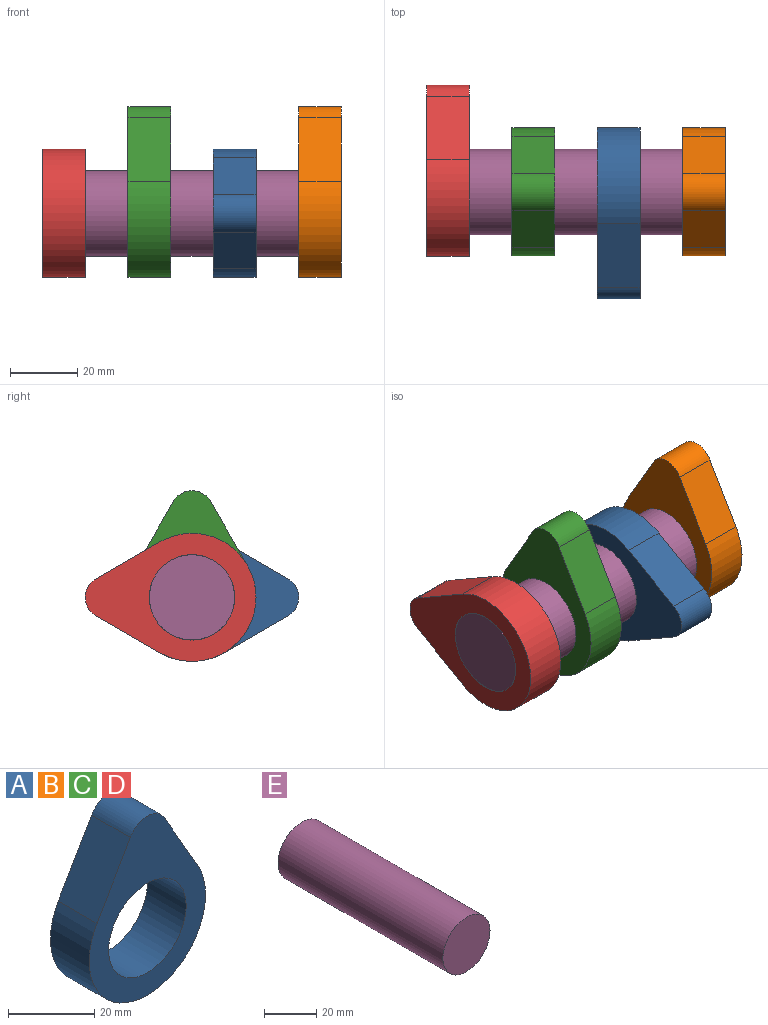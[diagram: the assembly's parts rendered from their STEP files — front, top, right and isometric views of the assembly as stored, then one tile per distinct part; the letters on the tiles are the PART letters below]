
ASSEMBLY  parts=5 mates=4
PART A: 7 faces, bbox 38.1x12.7x50.8 mm
  f0: cylinder r=6.35mm len=12.7mm, axis (0,1,0), area 173.1mm2, adj f1,f4,f5,f6
  f1: plane 18.9x12.7mm, normal (-0.87,0,0.5), area 277.2mm2, adj f0,f2,f5,f6
  f2: cylinder r=19.05mm len=38.1mm, axis (0,1,0), area 1013.5mm2, adj f1,f4,f5,f6
  f3: cylinder r=12.7mm len=25.4mm, axis (0,1,0), area 1013.4mm2, adj f5,f6
  f4: plane 18.9x12.7mm, normal (0.87,0,0.5), area 277.2mm2, adj f0,f2,f5,f6
  f5: plane 50.8x38.1mm, normal (0,-1,0), area 854.3mm2, adj f0,f1,f2,f3,f4
  f6: plane 50.8x38.1mm, normal (0,1,0), area 854.3mm2, adj f0,f1,f2,f3,f4
PART B: same geometry as A
PART C: same geometry as A
PART D: same geometry as A
PART E: 3 faces, bbox 25.4x88.9x25.4 mm
  f0: cylinder r=12.7mm len=88.9mm, axis (0,1,0), area 7093.9mm2, adj f1,f2
  f1: plane 25.4x25.4mm, normal (0,-1,0), area 506.7mm2, adj f0
  f2: plane 25.4x25.4mm, normal (0,1,0), area 506.7mm2, adj f0
PLACE A rot(axis=(0.58,0.58,-0.58),120deg) t=(12.7,0,0)mm
PLACE B rot(axis=(0,0,-1),90deg) t=(38.1,0,0)mm
PLACE C rot(axis=(0,0,-1),90deg) t=(-12.7,0,0)mm
PLACE D rot(axis=(-0.58,-0.58,-0.58),120deg) t=(-38.1,0,0)mm
PLACE E rot(axis=(0.58,0.58,-0.58),120deg) t=(0,0,0)mm
MATE fastened B.f3 <-> A.f3  axis (1,0,0) through (31.75,0,0)mm
MATE fastened D.f3 <-> E.f0  axis (-1,0,0) through (-44.45,0,0)mm
MATE fastened C.f3 <-> D.f3  axis (-1,0,0) through (-19.05,0,0)mm
MATE fastened A.f3 <-> C.f2  axis (-1,0,0) through (6.35,0,0)mm
